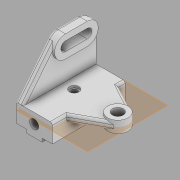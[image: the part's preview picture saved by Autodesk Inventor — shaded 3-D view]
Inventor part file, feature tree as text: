
AUTODESK INVENTOR PART (.ipt)
format: ipt  version: 2020 (Build 240168000, 168)  size: 251,392 bytes
history: native  units: mm
features: sketch x10, extrude x8, plane x1, hole x1, fillet x1
ambient origin geometry x8: Origin, YZ Plane, XZ Plane, XY Plane, X Axis, Y Axis, Z Axis, Center Point
bodies: Solid1 (feature_tree)
feature tree (21):
  extrude  "Extrusion1"  Depth=22.0mm
  extrude  "Extrusion2"  Depth=30.0mm
  extrude  "Extrusion3"  Depth=100.0mm
  plane  "Work Plane1"
  extrude  "Extrusion4"  Depth=15.0mm
  extrude  "Extrusion5"  Depth=10.0mm
  sketch  "Sketch6"  dims[d16=14.0mm d17=35.0mm]
  extrude  "AgujeroSuperior"  Depth=35.0mm
  extrude  "AgujeroFrontal"  Depth=10.0mm TaperAngle=0.0deg
  extrude  "AgujeroCirculo"  Depth=16.0mm TaperAngle=0.0deg
  hole  "Agujero1"  [1 undecoded]
  fillet  "Empalme1"  Radius=15.0mm
  sketch  "Sketch1"  dims[d0=50.0mm d2=22.0mm]
  sketch  "Sketch2"  dims[d4=4.8mm d5=30.0mm]
  sketch  "Sketch3"  dims[d6=100.0mm d7=0.0mm d9=55.0mm]
  sketch  "Sketch4"  dims[d10=15.0mm d11=45.0mm]
  sketch  "Sketch5"  dims[d12=10.0mm d13=0.0mm d15=55.0mm]
  sketch  "Boceto7"  dims[d18=85.0mm d19=10.0mm d20=0.0mm]
  sketch  "Boceto8"  dims[d21=-5.0mm d22=16.0mm d23=0.0mm]
  sketch  "Boceto10"  dims[d24=30.0mm d25=3.0mm d26=0.0mm d27=15.0mm]
  sketch  "Boceto11"  dims[d30=30.0mm d31=13.0mm d32=0.0mm d33=55.0mm d35=12.7mm d37=12.5mm d38=11.0mm d39=16.0mm d40=100.0mm d41=0.0mm d47=15.0mm d48=28.0mm d49=16.0mm d50=0.0mm d52=13.0mm d53=25.0mm d54=35.0mm d55=9.0mm d56=6.0mm d57=13.0mm d58=3.0mm d59=90.0deg d60=8.0mm d61=20.594885mm d62=3.0mm]
note: 1 required parameter value undecoded (feature->parameter linkage not recoverable at this tier; creation-order binding heuristic only, values carry confidence <= 0.55)
